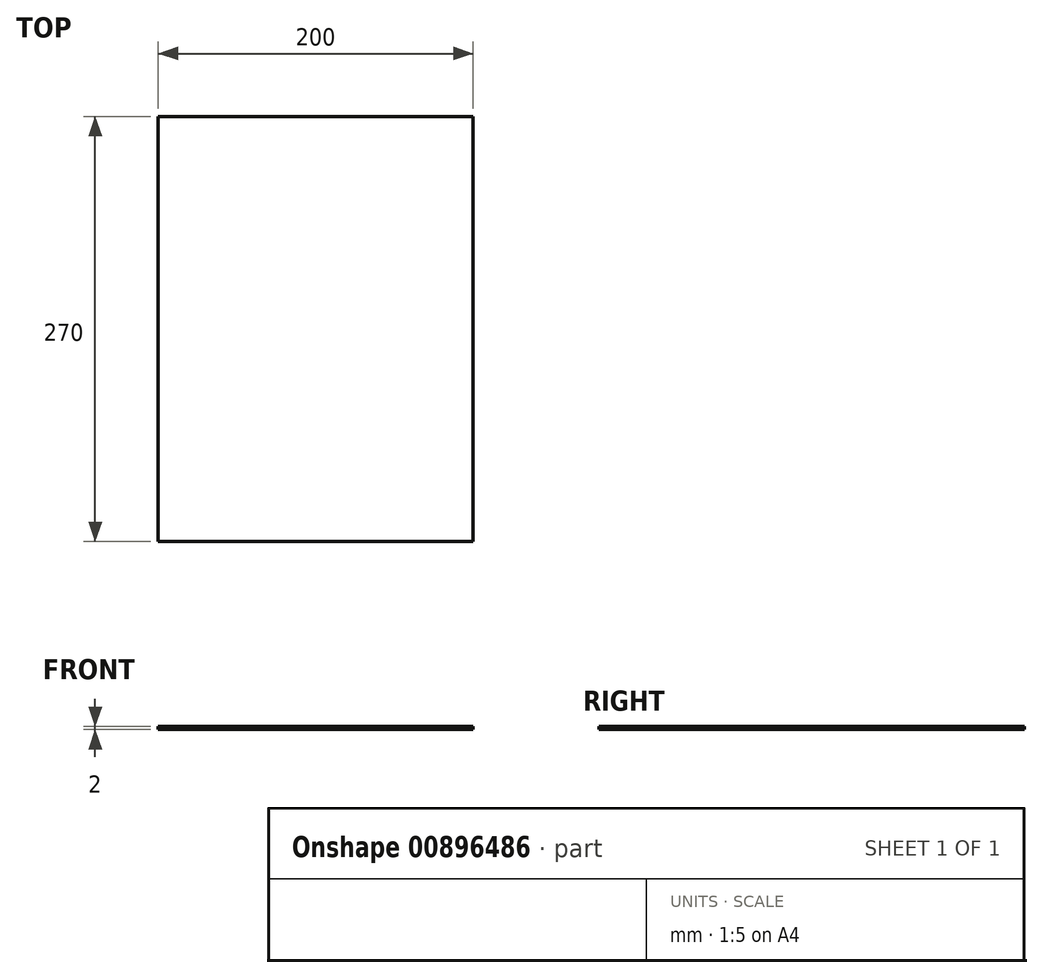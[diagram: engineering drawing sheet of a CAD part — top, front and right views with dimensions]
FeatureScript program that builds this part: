
annotation { "Feature Type Name" : "Feature", "Feature Type Description" : "" }
export const myFeature = defineFeature(function(context is Context, id is Id, definition is map)
    precondition{}
    {
        {
            var Q0;
            Q0=qCreatedBy(makeId("Top.planeOp"),FACE);
            var sketch = newSketch(context, id + "F0", { "sketchPlane" : qUnion([Q0])});
            skLineSegment(sketch, "E0.bottom", {"start": v(0, 0) * mm, "end": v(200, 0) * mm});
            skLineSegment(sketch, "E0.top", {"start": v(0, 270) * mm, "end": v(200, 270) * mm});
            skLineSegment(sketch, "E0.left", {"start": v(0, 0) * mm, "end": v(0, 270) * mm});
            skLineSegment(sketch, "E0.right", {"start": v(200, 0) * mm, "end": v(200, 270) * mm});
            skSolve(sketch);
        }
        {
            var Q0;
            Q0 = qSketchRegion(id + "F0", true);
            extrude(context, id + "F1", {"entities" : qUnion([Q0]), "depth" : 2 * mm, "offsetDistance" : 25 * mm});
        }
    });
